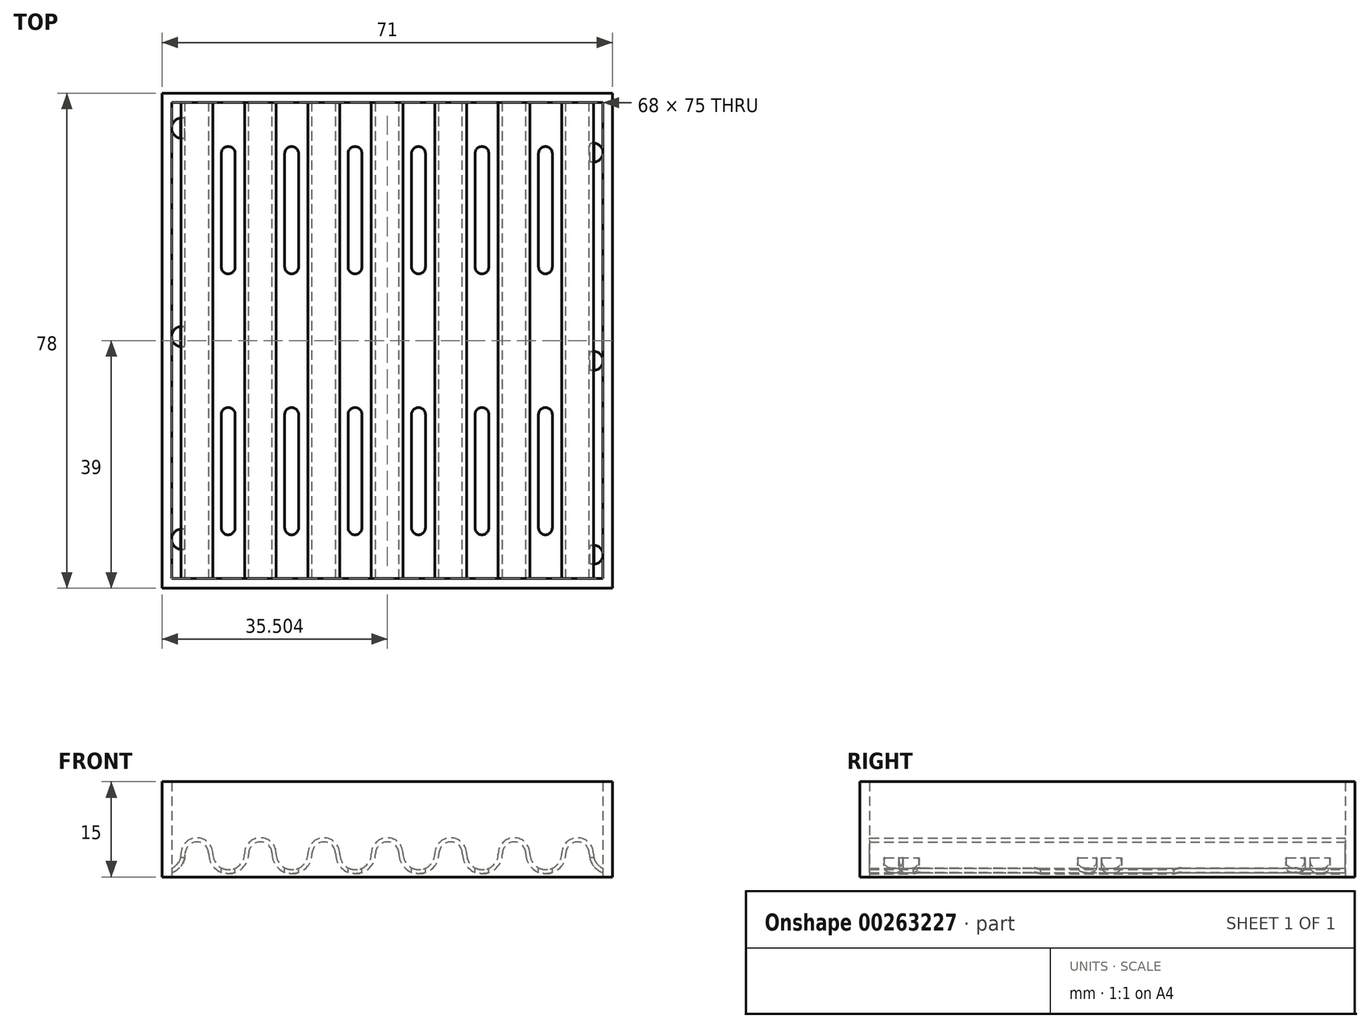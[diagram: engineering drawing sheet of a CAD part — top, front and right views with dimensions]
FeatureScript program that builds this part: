
annotation { "Feature Type Name" : "Feature", "Feature Type Description" : "" }
export const myFeature = defineFeature(function(context is Context, id is Id, definition is map)
    precondition{}
    {
        {
            var Q0;
            Q0=qCreatedBy(makeId("Front.planeOp"),FACE);
            var sketch = newSketch(context, id + "F0", { "sketchPlane" : qUnion([Q0])});
            skArc(sketch, "E0", {"start": v(-22.73, 3.66) * mm, "mid": v(-25.23, 6.16) * mm, "end": v(-27.73, 3.66) * mm});
            skArc(sketch, "E1", {"start": v(-22.73, 3.66) * mm, "mid": v(-20.23, 1.16) * mm, "end": v(-17.73, 3.66) * mm});
            skArc(sketch, "E2.1.0.0", {"start": v(-12.73, 3.66) * mm, "mid": v(-15.23, 6.16) * mm, "end": v(-17.73, 3.66) * mm});
            skArc(sketch, "E2.1.0.1", {"start": v(-12.73, 3.66) * mm, "mid": v(-10.23, 1.16) * mm, "end": v(-7.73, 3.66) * mm});
            skArc(sketch, "E2.2.0.0", {"start": v(-2.73, 3.66) * mm, "mid": v(-5.23, 6.16) * mm, "end": v(-7.73, 3.66) * mm});
            skArc(sketch, "E2.2.0.1", {"start": v(-2.73, 3.66) * mm, "mid": v(-0.23, 1.16) * mm, "end": v(2.27, 3.66) * mm});
            skArc(sketch, "E2.3.0.0", {"start": v(7.27, 3.66) * mm, "mid": v(4.77, 6.16) * mm, "end": v(2.27, 3.66) * mm});
            skArc(sketch, "E2.3.0.1", {"start": v(7.27, 3.66) * mm, "mid": v(9.77, 1.16) * mm, "end": v(12.27, 3.66) * mm});
            skArc(sketch, "E2.4.0.0", {"start": v(17.27, 3.66) * mm, "mid": v(14.77, 6.16) * mm, "end": v(12.27, 3.66) * mm});
            skArc(sketch, "E2.4.0.1", {"start": v(17.27, 3.66) * mm, "mid": v(19.77, 1.16) * mm, "end": v(22.27, 3.66) * mm});
            skArc(sketch, "E2.5.0.0", {"start": v(27.27, 3.66) * mm, "mid": v(24.77, 6.16) * mm, "end": v(22.27, 3.66) * mm});
            skArc(sketch, "E2.5.0.1", {"start": v(27.27, 3.66) * mm, "mid": v(29.77, 1.16) * mm, "end": v(32.27, 3.66) * mm});
            skArc(sketch, "E2.6.0.0", {"start": v(37.27, 3.66) * mm, "mid": v(34.77, 6.16) * mm, "end": v(32.27, 3.66) * mm});
            skArc(sketch, "E2.6.0.1", {"start": v(37.27, 3.66) * mm, "mid": v(39.77, 1.16) * mm, "end": v(42.27, 3.66) * mm});
            skArc(sketch, "E2.7.0.0", {"start": v(47.27, 3.66) * mm, "mid": v(44.77, 6.16) * mm, "end": v(42.27, 3.66) * mm});
            skArc(sketch, "E2.7.0.1", {"start": v(47.27, 3.66) * mm, "mid": v(49.77, 1.16) * mm, "end": v(52.27, 3.66) * mm});
            skArc(sketch, "E2.8.0.0", {"start": v(57.27, 3.66) * mm, "mid": v(54.77, 6.16) * mm, "end": v(52.27, 3.66) * mm});
            skArc(sketch, "E2.8.0.1", {"start": v(57.27, 3.66) * mm, "mid": v(59.77, 1.16) * mm, "end": v(62.27, 3.66) * mm});
            skArc(sketch, "E2.9.0.0", {"start": v(67.27, 3.66) * mm, "mid": v(64.77, 6.16) * mm, "end": v(62.27, 3.66) * mm});
            skArc(sketch, "E2.9.0.1", {"start": v(67.27, 3.66) * mm, "mid": v(69.77, 1.16) * mm, "end": v(72.27, 3.66) * mm});
            skLineSegment(sketch, "E2.direction1", {"start": v(-27.73, 3.66) * mm, "end": v(-17.73, 3.66) * mm, "construction": true});
            skArc(sketch, "E3.0", {"start": v(-23.38, 3.66) * mm, "mid": v(-25.23, 5.51) * mm, "end": v(-27.08, 3.66) * mm});
            skArc(sketch, "E3.1", {"start": v(-23.38, 3.66) * mm, "mid": v(-20.23, 0.51) * mm, "end": v(-17.08, 3.66) * mm});
            skArc(sketch, "E3.2", {"start": v(-13.38, 3.66) * mm, "mid": v(-15.23, 5.51) * mm, "end": v(-17.08, 3.66) * mm});
            skArc(sketch, "E3.3", {"start": v(-13.38, 3.66) * mm, "mid": v(-10.23, 0.51) * mm, "end": v(-7.08, 3.66) * mm});
            skArc(sketch, "E3.4", {"start": v(-3.38, 3.66) * mm, "mid": v(-5.23, 5.51) * mm, "end": v(-7.08, 3.66) * mm});
            skArc(sketch, "E3.5", {"start": v(-3.38, 3.66) * mm, "mid": v(-0.23, 0.51) * mm, "end": v(2.92, 3.66) * mm});
            skArc(sketch, "E3.6", {"start": v(6.62, 3.66) * mm, "mid": v(4.77, 5.51) * mm, "end": v(2.92, 3.66) * mm});
            skArc(sketch, "E3.7", {"start": v(6.62, 3.66) * mm, "mid": v(9.77, 0.51) * mm, "end": v(12.92, 3.66) * mm});
            skArc(sketch, "E3.8", {"start": v(16.62, 3.66) * mm, "mid": v(14.77, 5.51) * mm, "end": v(12.92, 3.66) * mm});
            skArc(sketch, "E3.9", {"start": v(16.62, 3.66) * mm, "mid": v(19.77, 0.51) * mm, "end": v(22.92, 3.66) * mm});
            skArc(sketch, "E3.10", {"start": v(56.62, 3.66) * mm, "mid": v(54.77, 5.51) * mm, "end": v(52.92, 3.66) * mm});
            skArc(sketch, "E3.11", {"start": v(56.62, 3.66) * mm, "mid": v(59.77, 0.51) * mm, "end": v(62.92, 3.66) * mm});
            skArc(sketch, "E3.12", {"start": v(66.62, 3.66) * mm, "mid": v(64.77, 5.51) * mm, "end": v(62.92, 3.66) * mm});
            skArc(sketch, "E3.13", {"start": v(66.62, 3.66) * mm, "mid": v(69.77, 0.51) * mm, "end": v(72.92, 3.66) * mm});
            skArc(sketch, "E3.14", {"start": v(46.62, 3.66) * mm, "mid": v(49.77, 0.51) * mm, "end": v(52.92, 3.66) * mm});
            skArc(sketch, "E3.15", {"start": v(46.62, 3.66) * mm, "mid": v(44.77, 5.51) * mm, "end": v(42.92, 3.66) * mm});
            skArc(sketch, "E3.16", {"start": v(36.62, 3.66) * mm, "mid": v(39.77, 0.51) * mm, "end": v(42.92, 3.66) * mm});
            skArc(sketch, "E3.17", {"start": v(36.62, 3.66) * mm, "mid": v(34.77, 5.51) * mm, "end": v(32.92, 3.66) * mm});
            skArc(sketch, "E3.18", {"start": v(26.62, 3.66) * mm, "mid": v(29.77, 0.51) * mm, "end": v(32.92, 3.66) * mm});
            skArc(sketch, "E3.19", {"start": v(26.62, 3.66) * mm, "mid": v(24.77, 5.51) * mm, "end": v(22.92, 3.66) * mm});
            skLineSegment(sketch, "E4", {"start": v(-27.73, 3.66) * mm, "end": v(-27.08, 3.66) * mm});
            skLineSegment(sketch, "E5", {"start": v(72.27, 3.66) * mm, "end": v(72.92, 3.66) * mm});
            skSolve(sketch);
        }
        {
            var Q0;
            Q0 = qSketchRegion(id + "F0", true);
            extrude(context, id + "F1", {"entities" : qUnion([Q0]), "depth" : 75 * mm});
        }
        {
            var Q0;
            Q0=qCreatedBy(makeId("Front.planeOp"),FACE);
            var sketch = newSketch(context, id + "F2", { "sketchPlane" : qUnion([Q0])});
            skLineSegment(sketch, "E6.bottom", {"start": v(-9.23, 10.2) * mm, "end": v(58.77, 10.2) * mm});
            skLineSegment(sketch, "E6.top", {"start": v(-9.23, -4.87) * mm, "end": v(58.77, -4.87) * mm});
            skLineSegment(sketch, "E6.left", {"start": v(-9.23, 10.2) * mm, "end": v(-9.23, -4.87) * mm});
            skLineSegment(sketch, "E6.right", {"start": v(58.77, 10.2) * mm, "end": v(58.77, -4.87) * mm});
            skLineSegment(sketch, "E7.bottom", {"start": v(-43.2, 25.24) * mm, "end": v(107.99, 25.24) * mm});
            skLineSegment(sketch, "E7.top", {"start": v(-43.2, -15.9) * mm, "end": v(107.99, -15.9) * mm});
            skLineSegment(sketch, "E7.left", {"start": v(-43.2, 25.24) * mm, "end": v(-43.2, -15.9) * mm});
            skLineSegment(sketch, "E7.right", {"start": v(107.99, 25.24) * mm, "end": v(107.99, -15.9) * mm});
            skSolve(sketch);
        }
        {
            var Q0;
            Q0 = qSketchRegion(id + "F2", true);
            extrude(context, id + "F3", {"entities" : qUnion([Q0]), "operationType" : NewBodyOperationType.REMOVE, "endBound" : BoundingType.THROUGH_ALL, "depth" : 25 * mm});
        }
        {
            var Q0;
            Q0=qCreatedBy(makeId("Top.planeOp"),FACE);
            var sketch = newSketch(context, id + "F4", { "sketchPlane" : qUnion([Q0])});
            skLineSegment(sketch, "E8.left", {"start": v(-1.39, -8) * mm, "end": v(-1.39, -25.88) * mm});
            skLineSegment(sketch, "E8.right", {"start": v(0.79, -8) * mm, "end": v(0.79, -25.88) * mm});
            skLineSegment(sketch, "E9.left", {"start": v(-1.39, -49.12) * mm, "end": v(-1.39, -67) * mm});
            skLineSegment(sketch, "E9.right", {"start": v(0.79, -49.12) * mm, "end": v(0.79, -67) * mm});
            skArc(sketch, "E10", {"start": v(0.79, -8) * mm, "mid": v(-0.3, -6.91) * mm, "end": v(-1.39, -8) * mm});
            skArc(sketch, "E11", {"start": v(-1.39, -25.88) * mm, "mid": v(-0.3, -26.97) * mm, "end": v(0.79, -25.88) * mm});
            skArc(sketch, "E12", {"start": v(-1.39, -67) * mm, "mid": v(-0.3, -68.09) * mm, "end": v(0.79, -67) * mm});
            skArc(sketch, "E13", {"start": v(0.79, -49.12) * mm, "mid": v(-0.3, -48.03) * mm, "end": v(-1.39, -49.12) * mm});
            skLineSegment(sketch, "E14.1.0.0", {"start": v(8.61, -49.12) * mm, "end": v(8.61, -67) * mm});
            skLineSegment(sketch, "E14.1.0.1", {"start": v(8.61, -8) * mm, "end": v(8.61, -25.88) * mm});
            skLineSegment(sketch, "E14.1.0.2", {"start": v(10.79, -49.12) * mm, "end": v(10.79, -67) * mm});
            skLineSegment(sketch, "E14.1.0.3", {"start": v(10.79, -8) * mm, "end": v(10.79, -25.88) * mm});
            skArc(sketch, "E14.1.0.4", {"start": v(8.61, -25.88) * mm, "mid": v(9.7, -26.97) * mm, "end": v(10.79, -25.88) * mm});
            skArc(sketch, "E14.1.0.5", {"start": v(8.61, -67) * mm, "mid": v(9.7, -68.09) * mm, "end": v(10.79, -67) * mm});
            skArc(sketch, "E14.1.0.6", {"start": v(10.79, -49.12) * mm, "mid": v(9.7, -48.03) * mm, "end": v(8.61, -49.12) * mm});
            skArc(sketch, "E14.1.0.7", {"start": v(10.79, -8) * mm, "mid": v(9.7, -6.91) * mm, "end": v(8.61, -8) * mm});
            skLineSegment(sketch, "E14.2.0.0", {"start": v(18.61, -49.12) * mm, "end": v(18.61, -67) * mm});
            skLineSegment(sketch, "E14.2.0.1", {"start": v(18.61, -8) * mm, "end": v(18.61, -25.88) * mm});
            skLineSegment(sketch, "E14.2.0.2", {"start": v(20.79, -49.12) * mm, "end": v(20.79, -67) * mm});
            skLineSegment(sketch, "E14.2.0.3", {"start": v(20.79, -8) * mm, "end": v(20.79, -25.88) * mm});
            skArc(sketch, "E14.2.0.4", {"start": v(18.61, -25.88) * mm, "mid": v(19.7, -26.97) * mm, "end": v(20.79, -25.88) * mm});
            skArc(sketch, "E14.2.0.5", {"start": v(18.61, -67) * mm, "mid": v(19.7, -68.09) * mm, "end": v(20.79, -67) * mm});
            skArc(sketch, "E14.2.0.6", {"start": v(20.79, -49.12) * mm, "mid": v(19.7, -48.03) * mm, "end": v(18.61, -49.12) * mm});
            skArc(sketch, "E14.2.0.7", {"start": v(20.79, -8) * mm, "mid": v(19.7, -6.91) * mm, "end": v(18.61, -8) * mm});
            skLineSegment(sketch, "E14.3.0.0", {"start": v(28.61, -49.12) * mm, "end": v(28.61, -67) * mm});
            skLineSegment(sketch, "E14.3.0.1", {"start": v(28.61, -8) * mm, "end": v(28.61, -25.88) * mm});
            skLineSegment(sketch, "E14.3.0.2", {"start": v(30.79, -49.12) * mm, "end": v(30.79, -67) * mm});
            skLineSegment(sketch, "E14.3.0.3", {"start": v(30.79, -8) * mm, "end": v(30.79, -25.88) * mm});
            skArc(sketch, "E14.3.0.4", {"start": v(28.61, -25.88) * mm, "mid": v(29.7, -26.97) * mm, "end": v(30.79, -25.88) * mm});
            skArc(sketch, "E14.3.0.5", {"start": v(28.61, -67) * mm, "mid": v(29.7, -68.09) * mm, "end": v(30.79, -67) * mm});
            skArc(sketch, "E14.3.0.6", {"start": v(30.79, -49.12) * mm, "mid": v(29.7, -48.03) * mm, "end": v(28.61, -49.12) * mm});
            skArc(sketch, "E14.3.0.7", {"start": v(30.79, -8) * mm, "mid": v(29.7, -6.91) * mm, "end": v(28.61, -8) * mm});
            skLineSegment(sketch, "E14.4.0.0", {"start": v(38.61, -49.12) * mm, "end": v(38.61, -67) * mm});
            skLineSegment(sketch, "E14.4.0.1", {"start": v(38.61, -8) * mm, "end": v(38.61, -25.88) * mm});
            skLineSegment(sketch, "E14.4.0.2", {"start": v(40.79, -49.12) * mm, "end": v(40.79, -67) * mm});
            skLineSegment(sketch, "E14.4.0.3", {"start": v(40.79, -8) * mm, "end": v(40.79, -25.88) * mm});
            skArc(sketch, "E14.4.0.4", {"start": v(38.61, -25.88) * mm, "mid": v(39.7, -26.97) * mm, "end": v(40.79, -25.88) * mm});
            skArc(sketch, "E14.4.0.5", {"start": v(38.61, -67) * mm, "mid": v(39.7, -68.09) * mm, "end": v(40.79, -67) * mm});
            skArc(sketch, "E14.4.0.6", {"start": v(40.79, -49.12) * mm, "mid": v(39.7, -48.03) * mm, "end": v(38.61, -49.12) * mm});
            skArc(sketch, "E14.4.0.7", {"start": v(40.79, -8) * mm, "mid": v(39.7, -6.91) * mm, "end": v(38.61, -8) * mm});
            skLineSegment(sketch, "E14.5.0.0", {"start": v(48.61, -49.12) * mm, "end": v(48.61, -67) * mm});
            skLineSegment(sketch, "E14.5.0.1", {"start": v(48.61, -8) * mm, "end": v(48.61, -25.88) * mm});
            skLineSegment(sketch, "E14.5.0.2", {"start": v(50.79, -49.12) * mm, "end": v(50.79, -67) * mm});
            skLineSegment(sketch, "E14.5.0.3", {"start": v(50.79, -8) * mm, "end": v(50.79, -25.88) * mm});
            skArc(sketch, "E14.5.0.4", {"start": v(48.61, -25.88) * mm, "mid": v(49.7, -26.97) * mm, "end": v(50.79, -25.88) * mm});
            skArc(sketch, "E14.5.0.5", {"start": v(48.61, -67) * mm, "mid": v(49.7, -68.09) * mm, "end": v(50.79, -67) * mm});
            skArc(sketch, "E14.5.0.6", {"start": v(50.79, -49.12) * mm, "mid": v(49.7, -48.03) * mm, "end": v(48.61, -49.12) * mm});
            skArc(sketch, "E14.5.0.7", {"start": v(50.79, -8) * mm, "mid": v(49.7, -6.91) * mm, "end": v(48.61, -8) * mm});
            skLineSegment(sketch, "E14.direction1", {"start": v(-1.39, -67) * mm, "end": v(8.61, -67) * mm, "construction": true});
            skSolve(sketch);
        }
        {
            var Q0;
            Q0 = qSketchRegion(id + "F4", true);
            extrude(context, id + "F5", {"entities" : qUnion([Q0]), "operationType" : NewBodyOperationType.REMOVE, "endBound" : BoundingType.SYMMETRIC, "oppositeDirection" : true, "depth" : 25 * mm});
        }
        {
            var Q0;
            Q0=qCreatedBy(makeId("Top.planeOp"),FACE);
            var sketch = newSketch(context, id + "F6", { "sketchPlane" : qUnion([Q0])});
            skLineSegment(sketch, "E15.bottom", {"start": v(-9.23, 0) * mm, "end": v(58.77, 0) * mm});
            skLineSegment(sketch, "E15.top", {"start": v(-9.23, -75) * mm, "end": v(58.77, -75) * mm});
            skLineSegment(sketch, "E15.left", {"start": v(-9.23, 0) * mm, "end": v(-9.23, -75) * mm});
            skLineSegment(sketch, "E15.right", {"start": v(58.77, 0) * mm, "end": v(58.77, -75) * mm});
            skLineSegment(sketch, "E16.bottom", {"start": v(-10.73, 1.5) * mm, "end": v(60.27, 1.5) * mm});
            skLineSegment(sketch, "E16.top", {"start": v(-10.73, -76.5) * mm, "end": v(60.27, -76.5) * mm});
            skLineSegment(sketch, "E16.left", {"start": v(-10.73, 1.5) * mm, "end": v(-10.73, -76.5) * mm});
            skLineSegment(sketch, "E16.right", {"start": v(60.27, 1.5) * mm, "end": v(60.27, -76.5) * mm});
            skSolve(sketch);
        }
        {
            var Q0;
            Q0 = qSketchRegion(id + "F6", true);
            extrude(context, id + "F7", {"entities" : qUnion([Q0]), "operationType" : NewBodyOperationType.ADD, "depth" : 15 * mm});
        }
        {
            var Q0;
            Q0=qCreatedBy(makeId("Top.planeOp"),FACE);
            var sketch = newSketch(context, id + "F8", { "sketchPlane" : qUnion([Q0])});
            skCircle(sketch, "E17", {"center": v(-7.61, -36.87) * mm, "radius": 1.61 * mm});
            skCircle(sketch, "E18", {"center": v(-7.61, -68.78) * mm, "radius": 1.61 * mm});
            skCircle(sketch, "E19", {"center": v(-7.61, -4.01) * mm, "radius": 1.61 * mm});
            skCircle(sketch, "E20", {"center": v(57.27, -7.87) * mm, "radius": 1.5 * mm});
            skCircle(sketch, "E21", {"center": v(57.27, -40.69) * mm, "radius": 1.5 * mm});
            skCircle(sketch, "E22", {"center": v(57.27, -71.22) * mm, "radius": 1.5 * mm});
            skSolve(sketch);
        }
        {
            var Q0;
            Q0 = qSketchRegion(id + "F8", true);
            extrude(context, id + "F9", {"entities" : qUnion([Q0]), "operationType" : NewBodyOperationType.REMOVE, "depth" : 3 * mm});
        }
    });
